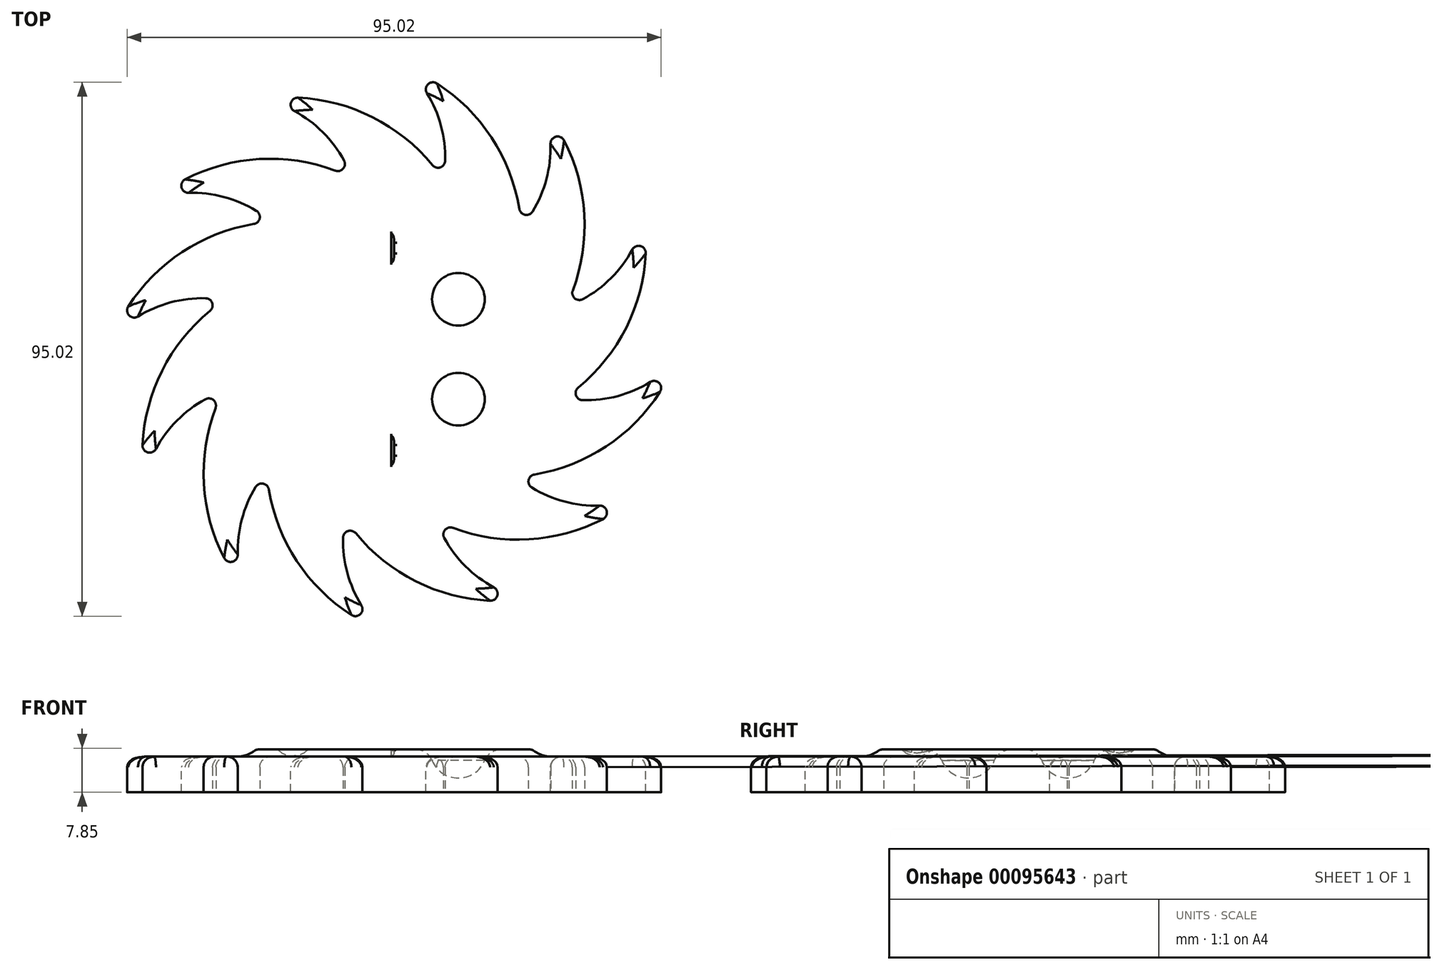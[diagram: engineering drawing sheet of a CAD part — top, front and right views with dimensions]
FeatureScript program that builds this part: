
annotation { "Feature Type Name" : "Feature", "Feature Type Description" : "" }
export const myFeature = defineFeature(function(context is Context, id is Id, definition is map)
    precondition{}
    {
        {
            var Q0;
            Q0=qCreatedBy(makeId("Top.planeOp"),FACE);
            var sketch = newSketch(context, id + "F0", { "sketchPlane" : qUnion([Q0])});
            skCircle(sketch, "E0", {"center": v(0, 0) * mm, "radius": 25.4 * mm});
            skArc(sketch, "E1", {"start": v(0, 25.4) * mm, "mid": v(-20.97, 33.88) * mm, "end": v(-42.45, 26.83) * mm});
            skPoint(sketch, "E1.first.point", {"position": v(0, 25.4) * mm});
            skPoint(sketch, "E1.second.point", {"position": v(-42.45, 26.83) * mm});
            skPoint(sketch, "E2.second.point", {"position": v(-17.77, 18.15) * mm});
            skArc(sketch, "E3.trimOffspring", {"start": v(-17.77, 18.15) * mm, "mid": v(-28.66, 26.6) * mm, "end": v(-42.45, 26.83) * mm});
            skArc(sketch, "E4.1.0", {"start": v(-12.7, 22) * mm, "mid": v(-35.1, 18.86) * mm, "end": v(-50.18, 2) * mm});
            skArc(sketch, "E4.1.1", {"start": v(-24.46, 6.83) * mm, "mid": v(-38.13, 8.71) * mm, "end": v(-50.18, 2) * mm});
            skArc(sketch, "E4.2.0", {"start": v(-22, 12.7) * mm, "mid": v(-39.82, -1.22) * mm, "end": v(-44.46, -23.35) * mm});
            skArc(sketch, "E4.2.1", {"start": v(-24.6, -6.32) * mm, "mid": v(-37.37, -11.52) * mm, "end": v(-44.46, -23.35) * mm});
            skArc(sketch, "E4.3.0", {"start": v(-25.4, 0) * mm, "mid": v(-33.88, -20.97) * mm, "end": v(-26.83, -42.45) * mm});
            skArc(sketch, "E4.3.1", {"start": v(-18.15, -17.77) * mm, "mid": v(-26.6, -28.66) * mm, "end": v(-26.83, -42.45) * mm});
            skArc(sketch, "E4.4.0", {"start": v(-22, -12.7) * mm, "mid": v(-18.86, -35.1) * mm, "end": v(-2, -50.18) * mm});
            skArc(sketch, "E4.4.1", {"start": v(-6.83, -24.46) * mm, "mid": v(-8.71, -38.13) * mm, "end": v(-2, -50.18) * mm});
            skArc(sketch, "E4.5.0", {"start": v(-12.7, -22) * mm, "mid": v(1.22, -39.82) * mm, "end": v(23.35, -44.46) * mm});
            skArc(sketch, "E4.5.1", {"start": v(6.32, -24.6) * mm, "mid": v(11.52, -37.37) * mm, "end": v(23.35, -44.46) * mm});
            skArc(sketch, "E4.6.0", {"start": v(0, -25.4) * mm, "mid": v(20.97, -33.88) * mm, "end": v(42.45, -26.83) * mm});
            skArc(sketch, "E4.6.1", {"start": v(17.77, -18.15) * mm, "mid": v(28.66, -26.6) * mm, "end": v(42.45, -26.83) * mm});
            skArc(sketch, "E4.7.0", {"start": v(12.7, -22) * mm, "mid": v(35.1, -18.86) * mm, "end": v(50.18, -2) * mm});
            skArc(sketch, "E4.7.1", {"start": v(24.46, -6.83) * mm, "mid": v(38.13, -8.71) * mm, "end": v(50.18, -2) * mm});
            skArc(sketch, "E4.8.0", {"start": v(22, -12.7) * mm, "mid": v(39.82, 1.22) * mm, "end": v(44.46, 23.35) * mm});
            skArc(sketch, "E4.8.1", {"start": v(24.6, 6.32) * mm, "mid": v(37.37, 11.52) * mm, "end": v(44.46, 23.35) * mm});
            skArc(sketch, "E4.9.0", {"start": v(25.4, 0) * mm, "mid": v(33.88, 20.97) * mm, "end": v(26.83, 42.45) * mm});
            skArc(sketch, "E4.9.1", {"start": v(18.15, 17.77) * mm, "mid": v(26.6, 28.66) * mm, "end": v(26.83, 42.45) * mm});
            skArc(sketch, "E4.10.0", {"start": v(22, 12.7) * mm, "mid": v(18.86, 35.1) * mm, "end": v(2, 50.18) * mm});
            skArc(sketch, "E4.10.1", {"start": v(6.83, 24.46) * mm, "mid": v(8.71, 38.13) * mm, "end": v(2, 50.18) * mm});
            skArc(sketch, "E4.11.0", {"start": v(12.7, 22) * mm, "mid": v(-1.22, 39.82) * mm, "end": v(-23.35, 44.46) * mm});
            skArc(sketch, "E4.11.1", {"start": v(-6.32, 24.6) * mm, "mid": v(-11.52, 37.37) * mm, "end": v(-23.35, 44.46) * mm});
            skSolve(sketch);
        }
        {
            var Q0;
            {var subQ0=sQuery(id+"F0.wireOp",EDGE,"E0");var subQ1=makeQuery(id+"F0.imprint","INTERSECT",VERTEX,{"derivedFrom":[subQ0,sQuery(id+"F0.wireOp",EDGE,"E1")]});Q0=makeQuery(id+"F0.imprint","IMPRINT",FACE,{"disambiguationData":[TD([[makeQuery(id+"F0.imprint","IMPRINT",EDGE,{"disambiguationData":[TD([[subQ1,-1.0]])],"derivedFrom":subQ0}),1.0]])]});}
            extrude(context, id + "F1", {"entities" : qUnion([Q0]), "depth" : 7.62 * mm});
        }
        {
            var Q0;
            {var subQ0=sQuery(id+"F0.wireOp",EDGE,"E1");Q0=makeQuery(id+"F0.imprint","IMPRINT",FACE,{"disambiguationData":[TD([[makeQuery(id+"F0.imprint","IMPRINT",EDGE,{"derivedFrom":subQ0}),1.0]])]});}
            var Q1;
            {var subQ0=sQuery(id+"F0.wireOp",EDGE,"E4.1.0");var subQ1=sQuery(id+"F0.wireOp",EDGE,"E0");var subQ2=makeQuery(id+"F0.imprint","INTERSECT",VERTEX,{"derivedFrom":[subQ1,subQ0]});Q1=makeQuery(id+"F0.imprint","IMPRINT",FACE,{"disambiguationData":[TD([[makeQuery(id+"F0.imprint","IMPRINT",EDGE,{"disambiguationData":[TD([[subQ2,1.0]])],"derivedFrom":subQ1}),-1.0]])]});}
            var Q2;
            {var subQ5=sQuery(id+"F0.wireOp",EDGE,"E3.trimOffspring");var subQ7=sQuery(id+"F0.wireOp",EDGE,"E0");var subQ8=makeQuery(id+"F0.imprint","INTERSECT",VERTEX,{"derivedFrom":[subQ7,subQ5]});Q2=makeQuery(id+"F0.imprint","IMPRINT",FACE,{"disambiguationData":[TD([[makeQuery(id+"F0.imprint","IMPRINT",EDGE,{"disambiguationData":[TD([[subQ8,-1.0]])],"derivedFrom":subQ7}),-1.0]])]});}
            var Q3;
            {var subQ5=sQuery(id+"F0.wireOp",EDGE,"E4.1.1");var subQ7=sQuery(id+"F0.wireOp",EDGE,"E0");var subQ8=makeQuery(id+"F0.imprint","INTERSECT",VERTEX,{"derivedFrom":[subQ7,subQ5]});Q3=makeQuery(id+"F0.imprint","IMPRINT",FACE,{"disambiguationData":[TD([[makeQuery(id+"F0.imprint","IMPRINT",EDGE,{"disambiguationData":[TD([[subQ8,-1.0]])],"derivedFrom":subQ7}),-1.0]])]});}
            var Q4;
            {var subQ5=sQuery(id+"F0.wireOp",EDGE,"E4.2.1");var subQ7=sQuery(id+"F0.wireOp",EDGE,"E0");var subQ8=makeQuery(id+"F0.imprint","INTERSECT",VERTEX,{"derivedFrom":[subQ7,subQ5]});Q4=makeQuery(id+"F0.imprint","IMPRINT",FACE,{"disambiguationData":[TD([[makeQuery(id+"F0.imprint","IMPRINT",EDGE,{"disambiguationData":[TD([[subQ8,-1.0]])],"derivedFrom":subQ7}),-1.0]])]});}
            var Q5;
            {var subQ3=sQuery(id+"F0.wireOp",EDGE,"E4.3.1");var subQ5=sQuery(id+"F0.wireOp",EDGE,"E0");var subQ6=makeQuery(id+"F0.imprint","INTERSECT",VERTEX,{"derivedFrom":[subQ5,subQ3]});Q5=makeQuery(id+"F0.imprint","IMPRINT",FACE,{"disambiguationData":[TD([[makeQuery(id+"F0.imprint","IMPRINT",EDGE,{"disambiguationData":[TD([[subQ6,-1.0]])],"derivedFrom":subQ5}),-1.0]])]});}
            var Q6;
            {var subQ5=sQuery(id+"F0.wireOp",EDGE,"E4.4.1");var subQ7=sQuery(id+"F0.wireOp",EDGE,"E0");var subQ8=makeQuery(id+"F0.imprint","INTERSECT",VERTEX,{"derivedFrom":[subQ7,subQ5]});Q6=makeQuery(id+"F0.imprint","IMPRINT",FACE,{"disambiguationData":[TD([[makeQuery(id+"F0.imprint","IMPRINT",EDGE,{"disambiguationData":[TD([[subQ8,-1.0]])],"derivedFrom":subQ7}),-1.0]])]});}
            var Q7;
            {var subQ0=sQuery(id+"F0.wireOp",EDGE,"E4.5.1");var subQ1=sQuery(id+"F0.wireOp",EDGE,"E0");var subQ2=makeQuery(id+"F0.imprint","INTERSECT",VERTEX,{"derivedFrom":[subQ1,subQ0]});Q7=makeQuery(id+"F0.imprint","IMPRINT",FACE,{"disambiguationData":[TD([[makeQuery(id+"F0.imprint","IMPRINT",EDGE,{"disambiguationData":[TD([[subQ2,-1.0]])],"derivedFrom":subQ1}),-1.0]])]});}
            var Q8;
            {var subQ5=sQuery(id+"F0.wireOp",EDGE,"E4.6.1");var subQ7=sQuery(id+"F0.wireOp",EDGE,"E0");var subQ8=makeQuery(id+"F0.imprint","INTERSECT",VERTEX,{"derivedFrom":[subQ7,subQ5]});Q8=makeQuery(id+"F0.imprint","IMPRINT",FACE,{"disambiguationData":[TD([[makeQuery(id+"F0.imprint","IMPRINT",EDGE,{"disambiguationData":[TD([[subQ8,-1.0]])],"derivedFrom":subQ7}),-1.0]])]});}
            var Q9;
            {var subQ5=sQuery(id+"F0.wireOp",EDGE,"E4.7.1");var subQ7=sQuery(id+"F0.wireOp",EDGE,"E0");var subQ8=makeQuery(id+"F0.imprint","INTERSECT",VERTEX,{"derivedFrom":[subQ7,subQ5]});Q9=makeQuery(id+"F0.imprint","IMPRINT",FACE,{"disambiguationData":[TD([[makeQuery(id+"F0.imprint","IMPRINT",EDGE,{"disambiguationData":[TD([[subQ8,-1.0]])],"derivedFrom":subQ7}),-1.0]])]});}
            var Q10;
            {var subQ5=sQuery(id+"F0.wireOp",EDGE,"E4.8.1");var subQ7=sQuery(id+"F0.wireOp",EDGE,"E0");var subQ8=makeQuery(id+"F0.imprint","INTERSECT",VERTEX,{"derivedFrom":[subQ7,subQ5]});Q10=makeQuery(id+"F0.imprint","IMPRINT",FACE,{"disambiguationData":[TD([[makeQuery(id+"F0.imprint","IMPRINT",EDGE,{"disambiguationData":[TD([[subQ8,-1.0]])],"derivedFrom":subQ7}),-1.0]])]});}
            var Q11;
            {var subQ5=sQuery(id+"F0.wireOp",EDGE,"E0");var subQ7=sQuery(id+"F0.wireOp",EDGE,"E4.9.1");var subQ9=makeQuery(id+"F0.imprint","INTERSECT",VERTEX,{"derivedFrom":[subQ5,subQ7]});Q11=makeQuery(id+"F0.imprint","IMPRINT",FACE,{"disambiguationData":[TD([[makeQuery(id+"F0.imprint","IMPRINT",EDGE,{"disambiguationData":[TD([[subQ9,-1.0]])],"derivedFrom":subQ5}),-1.0]])]});}
            var Q12;
            {var subQ5=sQuery(id+"F0.wireOp",EDGE,"E1");var subQ6=sQuery(id+"F0.wireOp",EDGE,"E0");var subQ7=makeQuery(id+"F0.imprint","INTERSECT",VERTEX,{"derivedFrom":[subQ6,subQ5]});Q12=makeQuery(id+"F0.imprint","IMPRINT",FACE,{"disambiguationData":[TD([[makeQuery(id+"F0.imprint","IMPRINT",EDGE,{"disambiguationData":[TD([[subQ7,1.0]])],"derivedFrom":subQ6}),-1.0]])]});}
            var Q13;
            {var subQ0=sQuery(id+"F0.wireOp",EDGE,"E3.trimOffspring");var subQ1=sQuery(id+"F0.wireOp",EDGE,"E0");var subQ2=makeQuery(id+"F0.imprint","INTERSECT",VERTEX,{"derivedFrom":[subQ1,subQ0]});Q13=makeQuery(id+"F0.imprint","IMPRINT",FACE,{"disambiguationData":[TD([[makeQuery(id+"F0.imprint","IMPRINT",EDGE,{"disambiguationData":[TD([[subQ2,1.0]])],"derivedFrom":subQ1}),-1.0]])]});}
            var Q14;
            {var subQ0=sQuery(id+"F0.wireOp",EDGE,"E4.1.1");var subQ1=sQuery(id+"F0.wireOp",EDGE,"E0");var subQ2=makeQuery(id+"F0.imprint","INTERSECT",VERTEX,{"derivedFrom":[subQ1,subQ0]});Q14=makeQuery(id+"F0.imprint","IMPRINT",FACE,{"disambiguationData":[TD([[makeQuery(id+"F0.imprint","IMPRINT",EDGE,{"disambiguationData":[TD([[subQ2,1.0]])],"derivedFrom":subQ1}),-1.0]])]});}
            var Q15;
            {var subQ0=sQuery(id+"F0.wireOp",EDGE,"E4.2.1");var subQ1=sQuery(id+"F0.wireOp",EDGE,"E0");var subQ2=makeQuery(id+"F0.imprint","INTERSECT",VERTEX,{"derivedFrom":[subQ1,subQ0]});Q15=makeQuery(id+"F0.imprint","IMPRINT",FACE,{"disambiguationData":[TD([[makeQuery(id+"F0.imprint","IMPRINT",EDGE,{"disambiguationData":[TD([[subQ2,1.0]])],"derivedFrom":subQ1}),-1.0]])]});}
            var Q16;
            {var subQ0=sQuery(id+"F0.wireOp",EDGE,"E4.3.1");var subQ1=sQuery(id+"F0.wireOp",EDGE,"E0");var subQ2=makeQuery(id+"F0.imprint","INTERSECT",VERTEX,{"derivedFrom":[subQ1,subQ0]});Q16=makeQuery(id+"F0.imprint","IMPRINT",FACE,{"disambiguationData":[TD([[makeQuery(id+"F0.imprint","IMPRINT",EDGE,{"disambiguationData":[TD([[subQ2,1.0]])],"derivedFrom":subQ1}),-1.0]])]});}
            var Q17;
            {var subQ0=sQuery(id+"F0.wireOp",EDGE,"E4.4.1");var subQ1=sQuery(id+"F0.wireOp",EDGE,"E0");var subQ2=makeQuery(id+"F0.imprint","INTERSECT",VERTEX,{"derivedFrom":[subQ1,subQ0]});Q17=makeQuery(id+"F0.imprint","IMPRINT",FACE,{"disambiguationData":[TD([[makeQuery(id+"F0.imprint","IMPRINT",EDGE,{"disambiguationData":[TD([[subQ2,1.0]])],"derivedFrom":subQ1}),-1.0]])]});}
            var Q18;
            {var subQ0=sQuery(id+"F0.wireOp",EDGE,"E4.5.1");var subQ1=sQuery(id+"F0.wireOp",EDGE,"E0");var subQ2=makeQuery(id+"F0.imprint","INTERSECT",VERTEX,{"derivedFrom":[subQ1,subQ0]});Q18=makeQuery(id+"F0.imprint","IMPRINT",FACE,{"disambiguationData":[TD([[makeQuery(id+"F0.imprint","IMPRINT",EDGE,{"disambiguationData":[TD([[subQ2,1.0]])],"derivedFrom":subQ1}),-1.0]])]});}
            var Q19;
            {var subQ0=sQuery(id+"F0.wireOp",EDGE,"E4.6.1");var subQ1=sQuery(id+"F0.wireOp",EDGE,"E0");var subQ2=makeQuery(id+"F0.imprint","INTERSECT",VERTEX,{"derivedFrom":[subQ1,subQ0]});Q19=makeQuery(id+"F0.imprint","IMPRINT",FACE,{"disambiguationData":[TD([[makeQuery(id+"F0.imprint","IMPRINT",EDGE,{"disambiguationData":[TD([[subQ2,1.0]])],"derivedFrom":subQ1}),-1.0]])]});}
            var Q20;
            {var subQ0=sQuery(id+"F0.wireOp",EDGE,"E4.7.1");var subQ1=sQuery(id+"F0.wireOp",EDGE,"E0");var subQ2=makeQuery(id+"F0.imprint","INTERSECT",VERTEX,{"derivedFrom":[subQ1,subQ0]});Q20=makeQuery(id+"F0.imprint","IMPRINT",FACE,{"disambiguationData":[TD([[makeQuery(id+"F0.imprint","IMPRINT",EDGE,{"disambiguationData":[TD([[subQ2,1.0]])],"derivedFrom":subQ1}),-1.0]])]});}
            var Q21;
            {var subQ0=sQuery(id+"F0.wireOp",EDGE,"E4.8.1");var subQ1=sQuery(id+"F0.wireOp",EDGE,"E0");var subQ2=makeQuery(id+"F0.imprint","INTERSECT",VERTEX,{"derivedFrom":[subQ1,subQ0]});Q21=makeQuery(id+"F0.imprint","IMPRINT",FACE,{"disambiguationData":[TD([[makeQuery(id+"F0.imprint","IMPRINT",EDGE,{"disambiguationData":[TD([[subQ2,1.0]])],"derivedFrom":subQ1}),-1.0]])]});}
            var Q22;
            {var subQ0=sQuery(id+"F0.wireOp",EDGE,"E4.9.1");var subQ1=sQuery(id+"F0.wireOp",EDGE,"E0");var subQ2=makeQuery(id+"F0.imprint","INTERSECT",VERTEX,{"derivedFrom":[subQ1,subQ0]});Q22=makeQuery(id+"F0.imprint","IMPRINT",FACE,{"disambiguationData":[TD([[makeQuery(id+"F0.imprint","IMPRINT",EDGE,{"disambiguationData":[TD([[subQ2,1.0]])],"derivedFrom":subQ1}),-1.0]])]});}
            var Q23;
            {var subQ0=sQuery(id+"F0.wireOp",EDGE,"E4.10.1");var subQ1=sQuery(id+"F0.wireOp",EDGE,"E0");var subQ2=makeQuery(id+"F0.imprint","INTERSECT",VERTEX,{"derivedFrom":[subQ1,subQ0]});Q23=makeQuery(id+"F0.imprint","IMPRINT",FACE,{"disambiguationData":[TD([[makeQuery(id+"F0.imprint","IMPRINT",EDGE,{"disambiguationData":[TD([[subQ2,1.0]])],"derivedFrom":subQ1}),-1.0]])]});}
            extrude(context, id + "F2", {"entities" : qUnion([Q0, Q1, Q2, Q3, Q4, Q5, Q6, Q7, Q8, Q9, Q10, Q11, Q12, Q13, Q14, Q15, Q16, Q17, Q18, Q19, Q20, Q21, Q22, Q23]), "depth" : 6.35 * mm});
        }
        {
            var Q0;
            Q0=makeQuery(id+"F1.opExtrude","CAP_EDGE",EDGE,{"disambiguationData":[OSD([sQuery(id+"F0.wireOp",EDGE,"E0")])],"isStart":false});
            fillet(context, id + "F3", {"entities" : qUnion([Q0]), "radius" : 1.27 * mm, "tangentPropagation" : true, "allowEdgeOverflow" : false});
        }
        {
            var Q0;
            Q0=makeQuery(id+"F2.opExtrude","SWEPT_BODY",BODY,{"disambiguationData":[OSD([sQuery(id+"F0.wireOp",EDGE,"E0"),sQuery(id+"F0.wireOp",EDGE,"E1"),sQuery(id+"F0.wireOp",EDGE,"E3.trimOffspring"),sQuery(id+"F0.wireOp",EDGE,"E4.1.0"),sQuery(id+"F0.wireOp",EDGE,"E4.1.1"),sQuery(id+"F0.wireOp",EDGE,"E4.2.0"),sQuery(id+"F0.wireOp",EDGE,"E4.2.1"),sQuery(id+"F0.wireOp",EDGE,"E4.3.0"),sQuery(id+"F0.wireOp",EDGE,"E4.3.1"),sQuery(id+"F0.wireOp",EDGE,"E4.4.0"),sQuery(id+"F0.wireOp",EDGE,"E4.4.1"),sQuery(id+"F0.wireOp",EDGE,"E4.5.0"),sQuery(id+"F0.wireOp",EDGE,"E4.5.1"),sQuery(id+"F0.wireOp",EDGE,"E4.6.0"),sQuery(id+"F0.wireOp",EDGE,"E4.6.1"),sQuery(id+"F0.wireOp",EDGE,"E4.7.0"),sQuery(id+"F0.wireOp",EDGE,"E4.7.1"),sQuery(id+"F0.wireOp",EDGE,"E4.8.0"),sQuery(id+"F0.wireOp",EDGE,"E4.8.1"),sQuery(id+"F0.wireOp",EDGE,"E4.9.0"),sQuery(id+"F0.wireOp",EDGE,"E4.9.1"),sQuery(id+"F0.wireOp",EDGE,"E4.10.0"),sQuery(id+"F0.wireOp",EDGE,"E4.10.1"),sQuery(id+"F0.wireOp",EDGE,"E4.11.0"),sQuery(id+"F0.wireOp",EDGE,"E4.11.1")])]});
            var Q1;
            Q1=makeQuery(id+"F1.opExtrude","SWEPT_BODY",BODY,{"disambiguationData":[OSD([sQuery(id+"F0.wireOp",EDGE,"E0")])]});
            booleanBodies(context, id + "F4", {"operationType" : BooleanOperationType.UNION, "tools" : qUnion([Q0, Q1])});
        }
        {
            var Q0;
            {var subQ0=sQuery(id+"F0.wireOp",EDGE,"E0");Q0=makeQuery(id+"F4.opBoolean","MERGE",EDGE,{"derivedFrom":[makeQuery(id+"F2.opExtrude","CAP_EDGE",EDGE,{"disambiguationData":[OSD([subQ0])],"isStart":false}),makeQuery(id+"F3.opFillet","BLEND_EDGE",EDGE,{"blendedFrom":[makeQuery(id+"F1.opExtrude","CAP_EDGE",EDGE,{"disambiguationData":[OSD([subQ0])],"isStart":false}),makeQuery(id+"F1.opExtrude","SWEPT_FACE",FACE,{"disambiguationData":[OSD([subQ0])]})],"blendedInto":[makeQuery(id+"F1.opExtrude","SWEPT_FACE",FACE,{"disambiguationData":[OSD([subQ0])]})]})]});}
            fillet(context, id + "F5", {"entities" : qUnion([Q0]), "radius" : 5.08 * mm, "tangentPropagation" : true, "allowEdgeOverflow" : false});
        }
        {
            var Q0;
            Q0=qCreatedBy(makeId("Top.planeOp"),FACE);
            cPlane(context, id + "F6", {"entities" : qUnion([Q0]), "cplaneType" : CPlaneType.OFFSET, "offset" : 7.62 * mm, "width" : 152.4 * mm, "height" : 152.4 * mm});
        }
        {
            var Q0;
            Q0=qCreatedBy(id+"F6.planeOp",FACE);
            var sketch = newSketch(context, id + "F7", { "sketchPlane" : qUnion([Q0])});
            skCircle(sketch, "E5", {"center": v(11.43, 8.9) * mm, "radius": 5.08 * mm});
            skCircle(sketch, "E6", {"center": v(11.43, -8.9) * mm, "radius": 5.08 * mm});
            skArc(sketch, "E7", {"start": v(0, 16.76) * mm, "mid": v(-16.76, 0) * mm, "end": v(0, -16.76) * mm});
            skLineSegment(sketch, "E8", {"start": v(16.51, 8.9) * mm, "end": v(6.35, 8.9) * mm});
            skLineSegment(sketch, "E9", {"start": v(16.51, -8.9) * mm, "end": v(6.35, -8.9) * mm});
            skSolve(sketch);
        }
        {
            var Q0;
            {var subQ0=sQuery(id+"F7.wireOp",EDGE,"E9");Q0=makeQuery(id+"F7.imprint","IMPRINT",FACE,{"disambiguationData":[TD([[makeQuery(id+"F7.imprint","IMPRINT",EDGE,{"derivedFrom":subQ0}),1.0]])]});}
            var Q1;
            Q1=sQuery(id+"F7.wireOp",EDGE,"E9");
            revolve(context, id + "F8", {"operationType" : NewBodyOperationType.REMOVE, "entities" : qUnion([Q0]), "axis" : qUnion([Q1]), "revolveType" : RevolveType.FULL, "oppositeDirection" : true});
        }
        {
            var Q0;
            {var subQ0=sQuery(id+"F7.wireOp",EDGE,"E8");Q0=makeQuery(id+"F7.imprint","IMPRINT",FACE,{"disambiguationData":[TD([[makeQuery(id+"F7.imprint","IMPRINT",EDGE,{"derivedFrom":subQ0}),-1.0]])]});}
            var Q1;
            Q1=sQuery(id+"F7.wireOp",EDGE,"E8");
            revolve(context, id + "F9", {"operationType" : NewBodyOperationType.REMOVE, "entities" : qUnion([Q0]), "axis" : qUnion([Q1]), "revolveType" : RevolveType.FULL, "oppositeDirection" : true});
        }
        {
            var Q0;
            Q0=qCreatedBy(makeId("Right.planeOp"),FACE);
            var sketch = newSketch(context, id + "F10", { "sketchPlane" : qUnion([Q0])});
            skPoint(sketch, "E10", {"position": v(18, 7.71) * mm});
            skCircle(sketch, "E11", {"center": v(18, 10.18) * mm, "radius": 3.72 * mm});
            skSolve(sketch);
        }
        {
            var Q0;
            Q0=makeQuery(id+"F10.imprint","IMPRINT",FACE,{"disambiguationData":[TD([[makeQuery(id+"F10.imprint","IMPRINT",EDGE,{"derivedFrom":sQuery(id+"F10.wireOp",EDGE,"E11")}),1.0]])]});
            var Q1;
            Q1=sQuery(id+"F7.wireOp",EDGE,"E7");
            sweep(context, id + "F11", {"operationType" : NewBodyOperationType.REMOVE, "profiles" : qUnion([Q0]), "path" : qUnion([Q1])});
        }
        {
            var Q0;
            Q0=makeQuery(id+"F11.boolean.opBoolean","INTERSECT",EDGE,{"disambiguationData":[OD(0.0)],"derivedFrom":[makeQuery(id+"F1.opExtrude","CAP_FACE",FACE,{"disambiguationData":[OSD([sQuery(id+"F0.wireOp",EDGE,"E0")])],"isStart":false}),makeQuery(id+"F11.opSweep","SWEPT_FACE",FACE,{"disambiguationData":[OSD([sQuery(id+"F7.wireOp",EDGE,"E7"),sQuery(id+"F10.wireOp",EDGE,"E11")])]})]});
            var Q1;
            Q1=makeQuery(id+"F11.boolean.opBoolean","INTERSECT",EDGE,{"disambiguationData":[OD(1.0)],"derivedFrom":[makeQuery(id+"F1.opExtrude","CAP_FACE",FACE,{"disambiguationData":[OSD([sQuery(id+"F0.wireOp",EDGE,"E0")])],"isStart":false}),makeQuery(id+"F11.opSweep","SWEPT_FACE",FACE,{"disambiguationData":[OSD([sQuery(id+"F7.wireOp",EDGE,"E7"),sQuery(id+"F10.wireOp",EDGE,"E11")])]})]});
            var Q2;
            Q2=makeQuery(id+"F11.boolean.opBoolean","INTERSECT",EDGE,{"derivedFrom":[makeQuery(id+"F1.opExtrude","CAP_FACE",FACE,{"disambiguationData":[OSD([sQuery(id+"F0.wireOp",EDGE,"E0")])],"isStart":false}),makeQuery(id+"F11.opSweep","CAP_FACE",FACE,{"disambiguationData":[OSD([sQuery(id+"F7.wireOp",VERTEX,"E7.end"),sQuery(id+"F10.wireOp",EDGE,"E11")])],"isStart":false})]});
            var Q3;
            Q3=makeQuery(id+"F11.boolean.opBoolean","INTERSECT",EDGE,{"derivedFrom":[makeQuery(id+"F1.opExtrude","CAP_FACE",FACE,{"disambiguationData":[OSD([sQuery(id+"F0.wireOp",EDGE,"E0")])],"isStart":false}),makeQuery(id+"F11.opSweep","CAP_FACE",FACE,{"disambiguationData":[OSD([sQuery(id+"F7.wireOp",VERTEX,"E7.start"),sQuery(id+"F10.wireOp",EDGE,"E11")])],"isStart":true})]});
            var Q4;
            Q4=makeQuery(id+"F11.boolean.opBoolean","COPY",EDGE,{"derivedFrom":makeQuery(id+"F11.opSweep","CAP_EDGE",EDGE,{"disambiguationData":[OSD([sQuery(id+"F7.wireOp",VERTEX,"E7.start"),sQuery(id+"F10.wireOp",EDGE,"E11")])],"isStart":true})});
            var Q5;
            Q5=makeQuery(id+"F11.boolean.opBoolean","COPY",EDGE,{"derivedFrom":makeQuery(id+"F11.opSweep","CAP_EDGE",EDGE,{"disambiguationData":[OSD([sQuery(id+"F7.wireOp",VERTEX,"E7.end"),sQuery(id+"F10.wireOp",EDGE,"E11")])],"isStart":false})});
            fillet(context, id + "F12", {"entities" : qUnion([Q0, Q1, Q2, Q3, Q4, Q5]), "radius" : 0.5 * mm, "tangentPropagation" : true, "allowEdgeOverflow" : false});
        }
        {
            var Q0;
            Q0=makeQuery(id+"F2.opExtrude","SWEPT_EDGE",EDGE,{"disambiguationData":[OSD([sQuery(id+"F0.wireOp",EDGE,"E1"),sQuery(id+"F0.wireOp",EDGE,"E4.11.1")])]});
            var Q1;
            Q1=makeQuery(id+"F2.opExtrude","SWEPT_EDGE",EDGE,{"disambiguationData":[OSD([sQuery(id+"F0.wireOp",EDGE,"E3.trimOffspring"),sQuery(id+"F0.wireOp",EDGE,"E4.1.0")])]});
            var Q2;
            Q2=makeQuery(id+"F2.opExtrude","SWEPT_EDGE",EDGE,{"disambiguationData":[OSD([sQuery(id+"F0.wireOp",EDGE,"E4.1.1"),sQuery(id+"F0.wireOp",EDGE,"E4.2.0")])]});
            var Q3;
            Q3=makeQuery(id+"F2.opExtrude","SWEPT_EDGE",EDGE,{"disambiguationData":[OSD([sQuery(id+"F0.wireOp",EDGE,"E4.2.1"),sQuery(id+"F0.wireOp",EDGE,"E4.3.0")])]});
            var Q4;
            Q4=makeQuery(id+"F2.opExtrude","SWEPT_EDGE",EDGE,{"disambiguationData":[OSD([sQuery(id+"F0.wireOp",EDGE,"E4.3.1"),sQuery(id+"F0.wireOp",EDGE,"E4.4.0")])]});
            var Q5;
            Q5=makeQuery(id+"F2.opExtrude","SWEPT_EDGE",EDGE,{"disambiguationData":[OSD([sQuery(id+"F0.wireOp",EDGE,"E4.3.0"),sQuery(id+"F0.wireOp",EDGE,"E4.3.1")])]});
            var Q6;
            Q6=makeQuery(id+"F2.opExtrude","SWEPT_EDGE",EDGE,{"disambiguationData":[OSD([sQuery(id+"F0.wireOp",EDGE,"E4.2.0"),sQuery(id+"F0.wireOp",EDGE,"E4.2.1")])]});
            var Q7;
            Q7=makeQuery(id+"F2.opExtrude","SWEPT_EDGE",EDGE,{"disambiguationData":[OSD([sQuery(id+"F0.wireOp",EDGE,"E4.1.0"),sQuery(id+"F0.wireOp",EDGE,"E4.1.1")])]});
            var Q8;
            Q8=makeQuery(id+"F2.opExtrude","SWEPT_EDGE",EDGE,{"disambiguationData":[OSD([sQuery(id+"F0.wireOp",EDGE,"E1"),sQuery(id+"F0.wireOp",EDGE,"E3.trimOffspring")])]});
            var Q9;
            Q9=makeQuery(id+"F2.opExtrude","SWEPT_EDGE",EDGE,{"disambiguationData":[OSD([sQuery(id+"F0.wireOp",EDGE,"E4.11.0"),sQuery(id+"F0.wireOp",EDGE,"E4.11.1")])]});
            var Q10;
            Q10=makeQuery(id+"F2.opExtrude","SWEPT_EDGE",EDGE,{"disambiguationData":[OSD([sQuery(id+"F0.wireOp",EDGE,"E4.10.1"),sQuery(id+"F0.wireOp",EDGE,"E4.11.0")])]});
            var Q11;
            Q11=makeQuery(id+"F2.opExtrude","SWEPT_EDGE",EDGE,{"disambiguationData":[OSD([sQuery(id+"F0.wireOp",EDGE,"E4.10.0"),sQuery(id+"F0.wireOp",EDGE,"E4.10.1")])]});
            var Q12;
            Q12=makeQuery(id+"F2.opExtrude","SWEPT_EDGE",EDGE,{"disambiguationData":[OSD([sQuery(id+"F0.wireOp",EDGE,"E4.9.1"),sQuery(id+"F0.wireOp",EDGE,"E4.10.0")])]});
            var Q13;
            Q13=makeQuery(id+"F2.opExtrude","SWEPT_EDGE",EDGE,{"disambiguationData":[OSD([sQuery(id+"F0.wireOp",EDGE,"E4.9.0"),sQuery(id+"F0.wireOp",EDGE,"E4.9.1")])]});
            var Q14;
            Q14=makeQuery(id+"F2.opExtrude","SWEPT_EDGE",EDGE,{"disambiguationData":[OSD([sQuery(id+"F0.wireOp",EDGE,"E4.8.1"),sQuery(id+"F0.wireOp",EDGE,"E4.9.0")])]});
            var Q15;
            Q15=makeQuery(id+"F2.opExtrude","SWEPT_EDGE",EDGE,{"disambiguationData":[OSD([sQuery(id+"F0.wireOp",EDGE,"E4.8.0"),sQuery(id+"F0.wireOp",EDGE,"E4.8.1")])]});
            var Q16;
            Q16=makeQuery(id+"F2.opExtrude","SWEPT_EDGE",EDGE,{"disambiguationData":[OSD([sQuery(id+"F0.wireOp",EDGE,"E4.7.1"),sQuery(id+"F0.wireOp",EDGE,"E4.8.0")])]});
            var Q17;
            Q17=makeQuery(id+"F2.opExtrude","SWEPT_EDGE",EDGE,{"disambiguationData":[OSD([sQuery(id+"F0.wireOp",EDGE,"E4.7.0"),sQuery(id+"F0.wireOp",EDGE,"E4.7.1")])]});
            var Q18;
            Q18=makeQuery(id+"F2.opExtrude","SWEPT_EDGE",EDGE,{"disambiguationData":[OSD([sQuery(id+"F0.wireOp",EDGE,"E4.6.1"),sQuery(id+"F0.wireOp",EDGE,"E4.7.0")])]});
            var Q19;
            Q19=makeQuery(id+"F2.opExtrude","SWEPT_EDGE",EDGE,{"disambiguationData":[OSD([sQuery(id+"F0.wireOp",EDGE,"E4.6.0"),sQuery(id+"F0.wireOp",EDGE,"E4.6.1")])]});
            var Q20;
            Q20=makeQuery(id+"F2.opExtrude","SWEPT_EDGE",EDGE,{"disambiguationData":[OSD([sQuery(id+"F0.wireOp",EDGE,"E4.5.1"),sQuery(id+"F0.wireOp",EDGE,"E4.6.0")])]});
            var Q21;
            Q21=makeQuery(id+"F2.opExtrude","SWEPT_EDGE",EDGE,{"disambiguationData":[OSD([sQuery(id+"F0.wireOp",EDGE,"E4.5.0"),sQuery(id+"F0.wireOp",EDGE,"E4.5.1")])]});
            var Q22;
            Q22=makeQuery(id+"F2.opExtrude","SWEPT_EDGE",EDGE,{"disambiguationData":[OSD([sQuery(id+"F0.wireOp",EDGE,"E4.4.1"),sQuery(id+"F0.wireOp",EDGE,"E4.5.0")])]});
            var Q23;
            Q23=makeQuery(id+"F2.opExtrude","SWEPT_EDGE",EDGE,{"disambiguationData":[OSD([sQuery(id+"F0.wireOp",EDGE,"E4.4.0"),sQuery(id+"F0.wireOp",EDGE,"E4.4.1")])]});
            fillet(context, id + "F13", {"entities" : qUnion([Q0, Q1, Q2, Q3, Q4, Q5, Q6, Q7, Q8, Q9, Q10, Q11, Q12, Q13, Q14, Q15, Q16, Q17, Q18, Q19, Q20, Q21, Q22, Q23]), "radius" : 1.27 * mm, "tangentPropagation" : true, "allowEdgeOverflow" : false});
        }
        {
            var Q0;
            Q0=makeQuery(id+"F8.boolean.opBoolean","INTERSECT",EDGE,{"derivedFrom":[makeQuery(id+"F1.opExtrude","CAP_FACE",FACE,{"disambiguationData":[OSD([sQuery(id+"F0.wireOp",EDGE,"E0")])],"isStart":false}),makeQuery(id+"F8.opRevolve","SWEPT_FACE",FACE,{"disambiguationData":[OSD([sQuery(id+"F7.wireOp",EDGE,"E6")])]})]});
            var Q1;
            Q1=makeQuery(id+"F9.boolean.opBoolean","INTERSECT",EDGE,{"derivedFrom":[makeQuery(id+"F1.opExtrude","CAP_FACE",FACE,{"disambiguationData":[OSD([sQuery(id+"F0.wireOp",EDGE,"E0")])],"isStart":false}),makeQuery(id+"F9.opRevolve","SWEPT_FACE",FACE,{"disambiguationData":[OSD([sQuery(id+"F7.wireOp",EDGE,"E5")])]})]});
            fillet(context, id + "F14", {"entities" : qUnion([Q0, Q1]), "radius" : 3.17 * mm, "tangentPropagation" : true, "allowEdgeOverflow" : false});
        }
        {
            var Q0;
            Q0=makeQuery(id+"F2.opExtrude","CAP_FACE",FACE,{"disambiguationData":[OSD([sQuery(id+"F0.wireOp",EDGE,"E0"),sQuery(id+"F0.wireOp",EDGE,"E1"),sQuery(id+"F0.wireOp",EDGE,"E3.trimOffspring"),sQuery(id+"F0.wireOp",EDGE,"E4.1.0"),sQuery(id+"F0.wireOp",EDGE,"E4.1.1"),sQuery(id+"F0.wireOp",EDGE,"E4.2.0"),sQuery(id+"F0.wireOp",EDGE,"E4.2.1"),sQuery(id+"F0.wireOp",EDGE,"E4.3.0"),sQuery(id+"F0.wireOp",EDGE,"E4.3.1"),sQuery(id+"F0.wireOp",EDGE,"E4.4.0"),sQuery(id+"F0.wireOp",EDGE,"E4.4.1"),sQuery(id+"F0.wireOp",EDGE,"E4.5.0"),sQuery(id+"F0.wireOp",EDGE,"E4.5.1"),sQuery(id+"F0.wireOp",EDGE,"E4.6.0"),sQuery(id+"F0.wireOp",EDGE,"E4.6.1"),sQuery(id+"F0.wireOp",EDGE,"E4.7.0"),sQuery(id+"F0.wireOp",EDGE,"E4.7.1"),sQuery(id+"F0.wireOp",EDGE,"E4.8.0"),sQuery(id+"F0.wireOp",EDGE,"E4.8.1"),sQuery(id+"F0.wireOp",EDGE,"E4.9.0"),sQuery(id+"F0.wireOp",EDGE,"E4.9.1"),sQuery(id+"F0.wireOp",EDGE,"E4.10.0"),sQuery(id+"F0.wireOp",EDGE,"E4.10.1"),sQuery(id+"F0.wireOp",EDGE,"E4.11.0"),sQuery(id+"F0.wireOp",EDGE,"E4.11.1")])],"isStart":false});
            fillet(context, id + "F15", {"entities" : qUnion([Q0]), "radius" : 1.9 * mm, "tangentPropagation" : true, "allowEdgeOverflow" : false});
        }
    });
